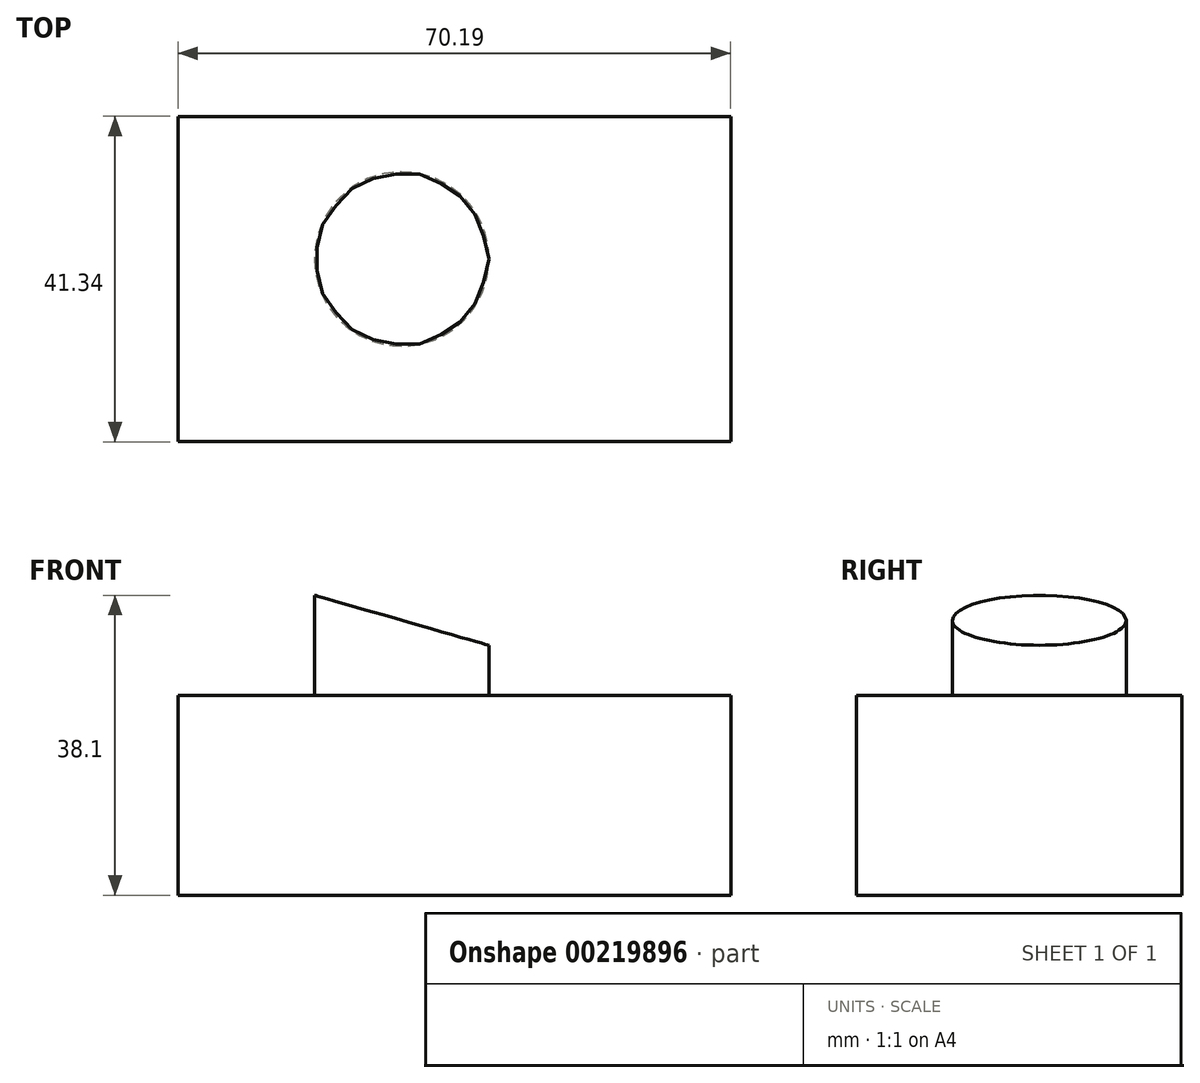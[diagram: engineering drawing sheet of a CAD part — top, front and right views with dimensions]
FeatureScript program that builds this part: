
annotation { "Feature Type Name" : "Feature", "Feature Type Description" : "" }
export const myFeature = defineFeature(function(context is Context, id is Id, definition is map)
    precondition{}
    {
        {
            var Q0;
            Q0=qCreatedBy(makeId("Top.planeOp"),FACE);
            var sketch = newSketch(context, id + "F0", { "sketchPlane" : qUnion([Q0])});
            skLineSegment(sketch, "E0.bottom", {"start": v(-28.4, 18.13) * mm, "end": v(41.8, 18.13) * mm});
            skLineSegment(sketch, "E0.top", {"start": v(-28.4, -23.2) * mm, "end": v(41.8, -23.2) * mm});
            skLineSegment(sketch, "E0.left", {"start": v(-28.4, 18.13) * mm, "end": v(-28.4, -23.2) * mm});
            skLineSegment(sketch, "E0.right", {"start": v(41.8, 18.13) * mm, "end": v(41.8, -23.2) * mm});
            skSolve(sketch);
        }
        {
            var Q0;
            Q0=makeQuery(id+"F0.imprint","IMPRINT",FACE,{"disambiguationData":[TD([[makeQuery(id+"F0.imprint","IMPRINT",EDGE,{"derivedFrom":sQuery(id+"F0.wireOp",EDGE,"E0.bottom")}),-1.0]])]});
            extrude(context, id + "F1", {"entities" : qUnion([Q0]), "depth" : 25.4 * mm});
        }
        {
            var Q0;
            Q0=makeQuery(id+"F1.opExtrude","CAP_FACE",FACE,{"disambiguationData":[OSD([sQuery(id+"F0.wireOp",EDGE,"E0.bottom"),sQuery(id+"F0.wireOp",EDGE,"E0.top"),sQuery(id+"F0.wireOp",EDGE,"E0.left"),sQuery(id+"F0.wireOp",EDGE,"E0.right")])],"isStart":false});
            var sketch = newSketch(context, id + "F2", { "sketchPlane" : qUnion([Q0])});
            skCircle(sketch, "E1", {"center": v(0, 0) * mm, "radius": 11.06 * mm});
            skSolve(sketch);
        }
        {
            var Q0;
            Q0 = qSketchRegion(id + "F2", true);
            extrude(context, id + "F3", {"entities" : qUnion([Q0]), "operationType" : NewBodyOperationType.ADD, "depth" : 12.7 * mm});
        }
        {
            var Q0;
            Q0=makeQuery(id+"F1.opExtrude","SWEPT_FACE",FACE,{"disambiguationData":[OSD([sQuery(id+"F0.wireOp",EDGE,"E0.top")])]});
            var sketch = newSketch(context, id + "F4", { "sketchPlane" : qUnion([Q0])});
            skLineSegment(sketch, "E2.0", {"start": v(-11.06, 38.1) * mm, "end": v(11.06, 38.1) * mm});
            skLineSegment(sketch, "E3", {"start": v(11.06, 38.1) * mm, "end": v(11.06, 31.75) * mm});
            skLineSegment(sketch, "E4", {"start": v(-11.06, 38.1) * mm, "end": v(11.06, 31.75) * mm});
            skPoint(sketch, "E5.orphan", {"position": v(11.06, 25.4) * mm});
            skSolve(sketch);
        }
        {
            var Q0;
            Q0 = qSketchRegion(id + "F4", true);
            extrude(context, id + "F5", {"entities" : qUnion([Q0]), "operationType" : NewBodyOperationType.REMOVE, "oppositeDirection" : true, "depth" : 58.67 * mm});
        }
    });
